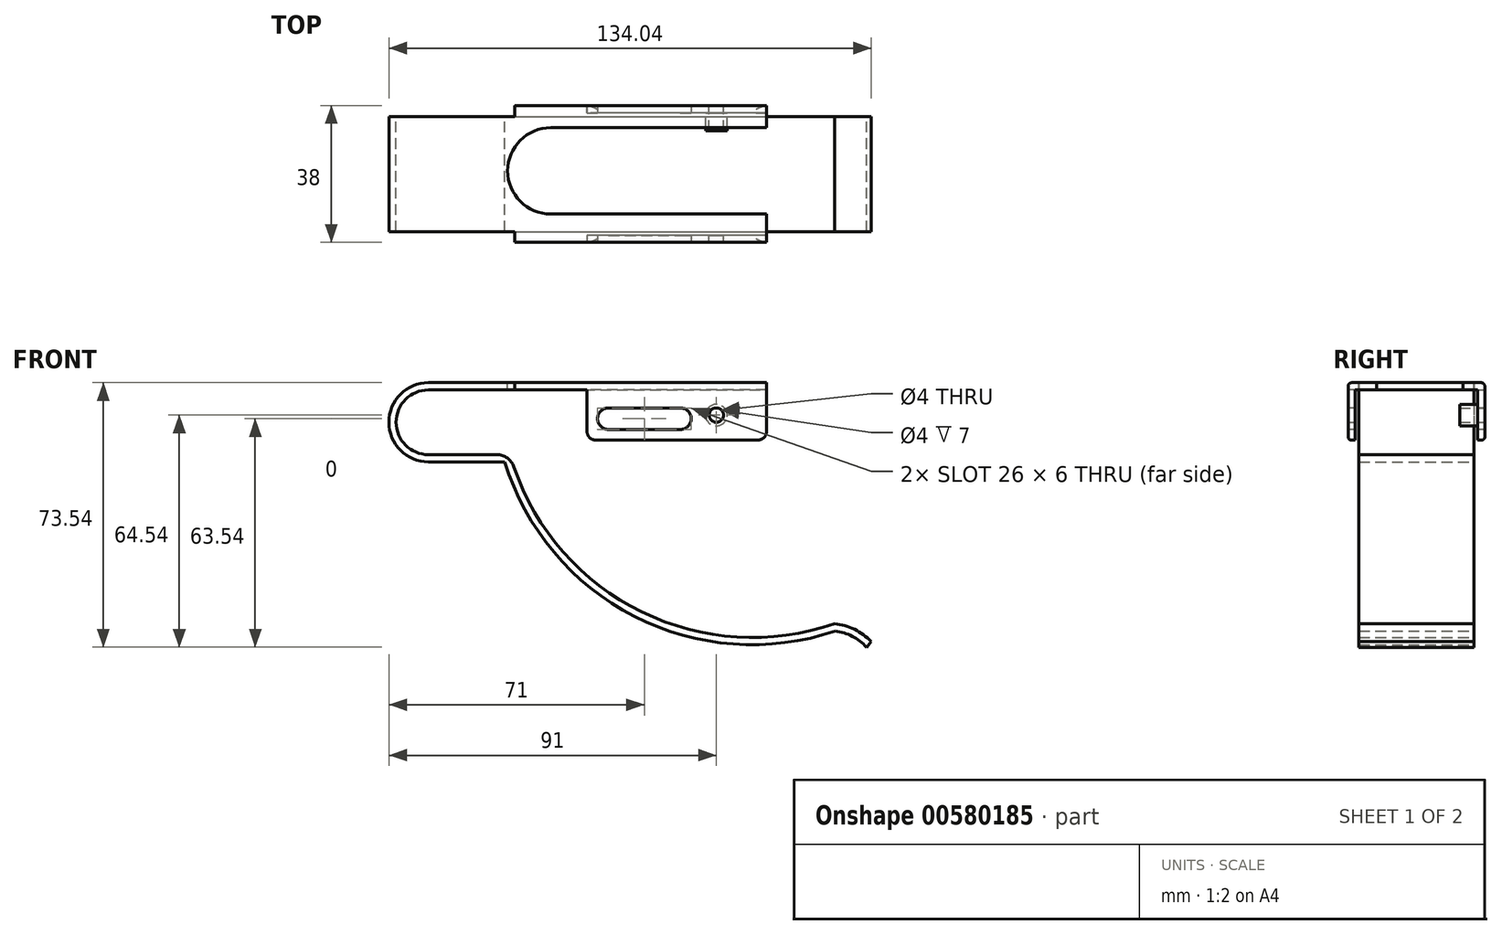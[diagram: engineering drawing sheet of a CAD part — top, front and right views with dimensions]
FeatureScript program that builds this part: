
annotation { "Feature Type Name" : "Feature", "Feature Type Description" : "" }
export const myFeature = defineFeature(function(context is Context, id is Id, definition is map)
    precondition{}
    {
        {
            var Q0;
            Q0=qCreatedBy(makeId("Front.planeOp"),FACE);
            var sketch = newSketch(context, id + "F0", { "sketchPlane" : qUnion([Q0])});
            skArc(sketch, "E0", {"start": v(0, 9) * mm, "mid": v(-9, 0) * mm, "end": v(0, -9) * mm});
            skLineSegment(sketch, "E1", {"start": v(0, 9) * mm, "end": v(94, 9) * mm});
            skLineSegment(sketch, "E2", {"start": v(0, -9) * mm, "end": v(19, -9) * mm});
            skArc(sketch, "E3", {"start": v(23.73, -12.39) * mm, "mid": v(59.23, -52.7) * mm, "end": v(112.85, -56) * mm});
            skArc(sketch, "E4", {"start": v(123.04, -61) * mm, "mid": v(118.4, -57.57) * mm, "end": v(112.85, -56) * mm});
            skPoint(sketch, "E5.visualSharp", {"position": v(22.67, -9) * mm});
            skArc(sketch, "E5.filletArc", {"start": v(23.73, -12.39) * mm, "mid": v(21.91, -9.93) * mm, "end": v(19, -9) * mm});
            skLineSegment(sketch, "E6.0", {"start": v(0, 11) * mm, "end": v(94, 11) * mm});
            skArc(sketch, "E6.1", {"start": v(121.74, -62.54) * mm, "mid": v(117.81, -59.51) * mm, "end": v(113.07, -58.04) * mm});
            skArc(sketch, "E6.2", {"start": v(21.18, -11) * mm, "mid": v(57.2, -53.93) * mm, "end": v(113.07, -58.04) * mm});
            skLineSegment(sketch, "E6.3", {"start": v(0, -11) * mm, "end": v(21.18, -11) * mm});
            skArc(sketch, "E6.4", {"start": v(0, 11) * mm, "mid": v(-11, 0) * mm, "end": v(0, -11) * mm});
            skLineSegment(sketch, "E7", {"start": v(94, 9) * mm, "end": v(94, 11) * mm});
            skLineSegment(sketch, "E8", {"start": v(121.74, -62.54) * mm, "end": v(123.04, -61) * mm});
            skLineSegment(sketch, "E9", {"start": v(123.04, -61) * mm, "end": v(154.31, -61) * mm, "construction": true});
            skSolve(sketch);
        }
        {
            var Q0;
            Q0 = qSketchRegion(id + "F0", true);
            extrude(context, id + "F1", {"entities" : qUnion([Q0]), "depth" : 16 * mm, "offsetDistance" : 25 * mm});
        }
        {
            var Q0;
            Q0=makeQuery(id+"F1.opExtrude","SWEPT_FACE",FACE,{"disambiguationData":[OSD([sQuery(id+"F0.wireOp",EDGE,"E6.0")])]});
            var sketch = newSketch(context, id + "F2", { "sketchPlane" : qUnion([Q0])});
            skLineSegment(sketch, "E10.bottom", {"start": v(94, 0) * mm, "end": v(24, 0) * mm});
            skLineSegment(sketch, "E10.top", {"start": v(94, 3) * mm, "end": v(24, 3) * mm});
            skLineSegment(sketch, "E10.left", {"start": v(94, 0) * mm, "end": v(94, 3) * mm});
            skLineSegment(sketch, "E10.right", {"start": v(24, 0) * mm, "end": v(24, 3) * mm});
            skSolve(sketch);
        }
        {
            var Q0;
            Q0=makeQuery(id+"F2.imprint","IMPRINT",FACE,{"disambiguationData":[TD([[makeQuery(id+"F2.imprint","IMPRINT",EDGE,{"derivedFrom":sQuery(id+"F2.wireOp",EDGE,"E10.bottom")}),1.0]])]});
            extrude(context, id + "F3", {"entities" : qUnion([Q0]), "operationType" : NewBodyOperationType.ADD, "oppositeDirection" : true, "depth" : 2 * mm, "offsetDistance" : 25 * mm});
        }
        {
            var Q0;
            Q0=makeQuery(id+"F3.opExtrude","SWEPT_FACE",FACE,{"disambiguationData":[OSD([sQuery(id+"F2.wireOp",EDGE,"E10.top")])]});
            var sketch = newSketch(context, id + "F4", { "sketchPlane" : qUnion([Q0])});
            skLineSegment(sketch, "E11.left", {"start": v(-94, 9) * mm, "end": v(-94, 9) * mm});
            skLineSegment(sketch, "E11.right", {"start": v(-24, 9) * mm, "end": v(-24, 9) * mm});
            skLineSegment(sketch, "E12.bottom", {"start": v(-94, 9) * mm, "end": v(-44, 9) * mm});
            skLineSegment(sketch, "E12.top", {"start": v(-94, -5) * mm, "end": v(-44, -5) * mm});
            skLineSegment(sketch, "E12.left", {"start": v(-94, 9) * mm, "end": v(-94, -5) * mm});
            skLineSegment(sketch, "E12.right", {"start": v(-44, 9) * mm, "end": v(-44, -5) * mm});
            skSolve(sketch);
        }
        {
            var Q0;
            Q0 = qSketchRegion(id + "F4", true);
            extrude(context, id + "F5", {"entities" : qUnion([Q0]), "operationType" : NewBodyOperationType.ADD, "oppositeDirection" : true, "depth" : 2 * mm, "offsetDistance" : 25 * mm});
        }
        {
            var Q0;
            Q0=makeQuery(id+"F3.opExtrude","CAP_EDGE",EDGE,{"disambiguationData":[OSD([sQuery(id+"F2.wireOp",EDGE,"E10.top")])],"isStart":true});
            var Q1;
            Q1=makeQuery(id+"F5.opExtrude","CAP_EDGE",EDGE,{"disambiguationData":[OSD([sQuery(id+"F4.wireOp",EDGE,"E12.top")])],"isStart":true});
            fillet(context, id + "F6", {"entities" : qUnion([Q0, Q1]), "radius" : 1 * mm, "tangentPropagation" : true, "allowEdgeOverflow" : false});
        }
        {
            var Q0;
            Q0=makeQuery(id+"F1.opExtrude","SWEPT_BODY",BODY,{"disambiguationData":[OSD([sQuery(id+"F0.wireOp",EDGE,"E0"),sQuery(id+"F0.wireOp",EDGE,"E1"),sQuery(id+"F0.wireOp",EDGE,"E2"),sQuery(id+"F0.wireOp",EDGE,"E3"),sQuery(id+"F0.wireOp",EDGE,"E4"),sQuery(id+"F0.wireOp",EDGE,"E5.filletArc"),sQuery(id+"F0.wireOp",EDGE,"E6.0"),sQuery(id+"F0.wireOp",EDGE,"E6.1"),sQuery(id+"F0.wireOp",EDGE,"E6.2"),sQuery(id+"F0.wireOp",EDGE,"E6.3"),sQuery(id+"F0.wireOp",EDGE,"E6.4"),sQuery(id+"F0.wireOp",EDGE,"E7"),sQuery(id+"F0.wireOp",EDGE,"E8")])]});
            var Q1;
            Q1=makeQuery(id+"F1.opExtrude","CAP_FACE",FACE,{"disambiguationData":[OSD([sQuery(id+"F0.wireOp",EDGE,"E0"),sQuery(id+"F0.wireOp",EDGE,"E1"),sQuery(id+"F0.wireOp",EDGE,"E2"),sQuery(id+"F0.wireOp",EDGE,"E3"),sQuery(id+"F0.wireOp",EDGE,"E4"),sQuery(id+"F0.wireOp",EDGE,"E5.filletArc"),sQuery(id+"F0.wireOp",EDGE,"E6.0"),sQuery(id+"F0.wireOp",EDGE,"E6.1"),sQuery(id+"F0.wireOp",EDGE,"E6.2"),sQuery(id+"F0.wireOp",EDGE,"E6.3"),sQuery(id+"F0.wireOp",EDGE,"E6.4"),sQuery(id+"F0.wireOp",EDGE,"E7"),sQuery(id+"F0.wireOp",EDGE,"E8")])],"isStart":false});
            mirror(context, id + "F7", {"operationType" : NewBodyOperationType.ADD, "entities" : qUnion([Q0]), "mirrorPlane" : qUnion([Q1])});
        }
        {
            var Q0;
            {var subQ0=makeQuery(id+"F3.boolean.opBoolean","MERGE",FACE,{"derivedFrom":[makeQuery(id+"F1.opExtrude","SWEPT_FACE",FACE,{"disambiguationData":[OSD([sQuery(id+"F0.wireOp",EDGE,"E6.0")])]}),makeQuery(id+"F3.opExtrude","CAP_FACE",FACE,{"disambiguationData":[OSD([sQuery(id+"F2.wireOp",EDGE,"E10.bottom"),sQuery(id+"F2.wireOp",EDGE,"E10.top"),sQuery(id+"F2.wireOp",EDGE,"E10.left"),sQuery(id+"F2.wireOp",EDGE,"E10.right")])],"isStart":true})]});Q0=makeQuery(id+"F7.boolean.opBoolean","MERGE",FACE,{"derivedFrom":[subQ0,makeQuery(id+"F7.opPattern","COPY",FACE,{"derivedFrom":subQ0,"instanceName":"1"})]});}
            var sketch = newSketch(context, id + "F8", { "sketchPlane" : qUnion([Q0])});
            skArc(sketch, "E13", {"start": v(34, -3.1) * mm, "mid": v(22, -15.1) * mm, "end": v(34, -27.1) * mm});
            skLineSegment(sketch, "E14", {"start": v(34, -3.1) * mm, "end": v(94, -3.1) * mm});
            skLineSegment(sketch, "E15", {"start": v(34, -27.1) * mm, "end": v(94, -27.1) * mm});
            skSolve(sketch);
        }
        {
            var Q0;
            Q0=makeQuery(id+"F8.imprint","IMPRINT",FACE,{"disambiguationData":[TD([[makeQuery(id+"F8.imprint","IMPRINT",EDGE,{"derivedFrom":sQuery(id+"F8.wireOp",EDGE,"E13")}),1.0]])]});
            extrude(context, id + "F9", {"entities" : qUnion([Q0]), "operationType" : NewBodyOperationType.REMOVE, "oppositeDirection" : true, "depth" : 2 * mm, "offsetDistance" : 25 * mm});
        }
        {
            var Q0;
            Q0=makeQuery(id+"F7.opPattern","COPY",FACE,{"derivedFrom":makeQuery(id+"F5.boolean.opBoolean","MERGE",FACE,{"derivedFrom":[makeQuery(id+"F3.opExtrude","SWEPT_FACE",FACE,{"disambiguationData":[OSD([sQuery(id+"F2.wireOp",EDGE,"E10.top")])]}),makeQuery(id+"F5.opExtrude","CAP_FACE",FACE,{"disambiguationData":[OSD([sQuery(id+"F4.wireOp",EDGE,"E12.bottom"),sQuery(id+"F4.wireOp",EDGE,"E12.top"),sQuery(id+"F4.wireOp",EDGE,"E12.left"),sQuery(id+"F4.wireOp",EDGE,"E12.right")])],"isStart":true})]}),"instanceName":"1"});
            var sketch = newSketch(context, id + "F10", { "sketchPlane" : qUnion([Q0])});
            skPoint(sketch, "E16.startSnap0", {"position": v(44, 2.5) * mm});
            skLineSegment(sketch, "E17", {"start": v(50, 1) * mm, "end": v(70, 1) * mm});
            skArc(sketch, "E18.0.startCap", {"start": v(50, -2) * mm, "mid": v(47, 1) * mm, "end": v(50, 4) * mm});
            skArc(sketch, "E18.0.endCap", {"start": v(70, 4) * mm, "mid": v(73, 1) * mm, "end": v(70, -2) * mm});
            skLineSegment(sketch, "E18.0.left", {"start": v(50, 4) * mm, "end": v(70, 4) * mm});
            skLineSegment(sketch, "E18.0.right", {"start": v(50, -2) * mm, "end": v(70, -2) * mm});
            skSolve(sketch);
        }
        {
            var Q0;
            Q0 = qSketchRegion(id + "F10", true);
            extrude(context, id + "F11", {"entities" : qUnion([Q0]), "operationType" : NewBodyOperationType.REMOVE, "endBound" : BoundingType.THROUGH_ALL, "oppositeDirection" : true, "depth" : 25 * mm, "offsetDistance" : 25 * mm});
        }
        {
            var Q0;
            Q0=makeQuery(id+"F5.boolean.opBoolean","MERGE",FACE,{"derivedFrom":[makeQuery(id+"F3.opExtrude","SWEPT_FACE",FACE,{"disambiguationData":[OSD([sQuery(id+"F2.wireOp",EDGE,"E10.top")])]}),makeQuery(id+"F5.opExtrude","CAP_FACE",FACE,{"disambiguationData":[OSD([sQuery(id+"F4.wireOp",EDGE,"E12.bottom"),sQuery(id+"F4.wireOp",EDGE,"E12.top"),sQuery(id+"F4.wireOp",EDGE,"E12.left"),sQuery(id+"F4.wireOp",EDGE,"E12.right")])],"isStart":true})]});
            var sketch = newSketch(context, id + "F12", { "sketchPlane" : qUnion([Q0])});
            skPoint(sketch, "E19", {"position": v(-80, 2) * mm});
            skSolve(sketch);
        }
        {
            var Q0;
            Q0=sQuery(id+"F12.wireOp",VERTEX,"E19");
            var Q1;
            Q1=makeQuery(id+"F1.opExtrude","SWEPT_BODY",BODY,{"disambiguationData":[OSD([sQuery(id+"F0.wireOp",EDGE,"E0"),sQuery(id+"F0.wireOp",EDGE,"E1"),sQuery(id+"F0.wireOp",EDGE,"E2"),sQuery(id+"F0.wireOp",EDGE,"E3"),sQuery(id+"F0.wireOp",EDGE,"E4"),sQuery(id+"F0.wireOp",EDGE,"E5.filletArc"),sQuery(id+"F0.wireOp",EDGE,"E6.0"),sQuery(id+"F0.wireOp",EDGE,"E6.1"),sQuery(id+"F0.wireOp",EDGE,"E6.2"),sQuery(id+"F0.wireOp",EDGE,"E6.3"),sQuery(id+"F0.wireOp",EDGE,"E6.4"),sQuery(id+"F0.wireOp",EDGE,"E7"),sQuery(id+"F0.wireOp",EDGE,"E8")])]});
            hole(context, id + "F13", {"style" : HoleStyle.SIMPLE, "endStyle" : HoleEndStyle.THROUGH, "holeDiameter" : 4 * mm, "majorDiameter" : 5 * mm, "isTappedThrough" : true, "tappedDepth" : 12 * mm, "tapClearance" : 3, "locations" : qUnion([Q0]), "scope" : qUnion([Q1])});
        }
        {
            var Q0;
            Q0=makeQuery(id+"F5.opExtrude","CAP_FACE",FACE,{"disambiguationData":[OSD([sQuery(id+"F4.wireOp",EDGE,"E12.bottom"),sQuery(id+"F4.wireOp",EDGE,"E12.top"),sQuery(id+"F4.wireOp",EDGE,"E12.left"),sQuery(id+"F4.wireOp",EDGE,"E12.right")])],"isStart":false});
            var sketch = newSketch(context, id + "F14", { "sketchPlane" : qUnion([Q0])});
            skCircle(sketch, "E20.0", {"center": v(80, 2) * mm, "radius": 2 * mm});
            skCircle(sketch, "E21.0", {"center": v(80, 2) * mm, "radius": 3 * mm});
            skLineSegment(sketch, "E22.0", {"start": v(39, 14) * mm, "end": v(39, -10) * mm});
            skLineSegment(sketch, "E22.1", {"start": v(99, 14) * mm, "end": v(39, 14) * mm});
            skLineSegment(sketch, "E22.2", {"start": v(99, -10) * mm, "end": v(99, 14) * mm});
            skLineSegment(sketch, "E22.3", {"start": v(39, -10) * mm, "end": v(99, -10) * mm});
            skSolve(sketch);
        }
        {
            var Q0;
            Q0=makeQuery(id+"F14.imprint","IMPRINT",FACE,{"disambiguationData":[TD([[makeQuery(id+"F14.imprint","IMPRINT",EDGE,{"derivedFrom":sQuery(id+"F14.wireOp",EDGE,"E20.0")}),-1.0]])]});
            extrude(context, id + "F15", {"entities" : qUnion([Q0]), "operationType" : NewBodyOperationType.ADD, "depth" : 5 * mm, "offsetDistance" : 25 * mm});
        }
        {
            var Q0;
            Q0=makeQuery(id+"F5.opExtrude","SWEPT_EDGE",EDGE,{"disambiguationData":[OSD([sQuery(id+"F4.wireOp",EDGE,"E12.top"),sQuery(id+"F4.wireOp",EDGE,"E12.right")])]});
            var Q1;
            Q1=makeQuery(id+"F7.opPattern","COPY",EDGE,{"derivedFrom":makeQuery(id+"F5.opExtrude","SWEPT_EDGE",EDGE,{"disambiguationData":[OSD([sQuery(id+"F4.wireOp",EDGE,"E12.top"),sQuery(id+"F4.wireOp",EDGE,"E12.right")])]}),"instanceName":"1"});
            var Q2;
            Q2=makeQuery(id+"F5.opExtrude","SWEPT_EDGE",EDGE,{"disambiguationData":[OSD([sQuery(id+"F4.wireOp",EDGE,"E12.top"),sQuery(id+"F4.wireOp",EDGE,"E12.left")])]});
            var Q3;
            Q3=makeQuery(id+"F7.opPattern","COPY",EDGE,{"derivedFrom":makeQuery(id+"F5.opExtrude","SWEPT_EDGE",EDGE,{"disambiguationData":[OSD([sQuery(id+"F4.wireOp",EDGE,"E12.top"),sQuery(id+"F4.wireOp",EDGE,"E12.left")])]}),"instanceName":"1"});
            fillet(context, id + "F16", {"entities" : qUnion([Q0, Q1, Q2, Q3]), "radius" : 3 * mm, "rho" : 0.5, "crossSection" : FilletCrossSection.CONIC, "allowEdgeOverflow" : false});
        }
    });
